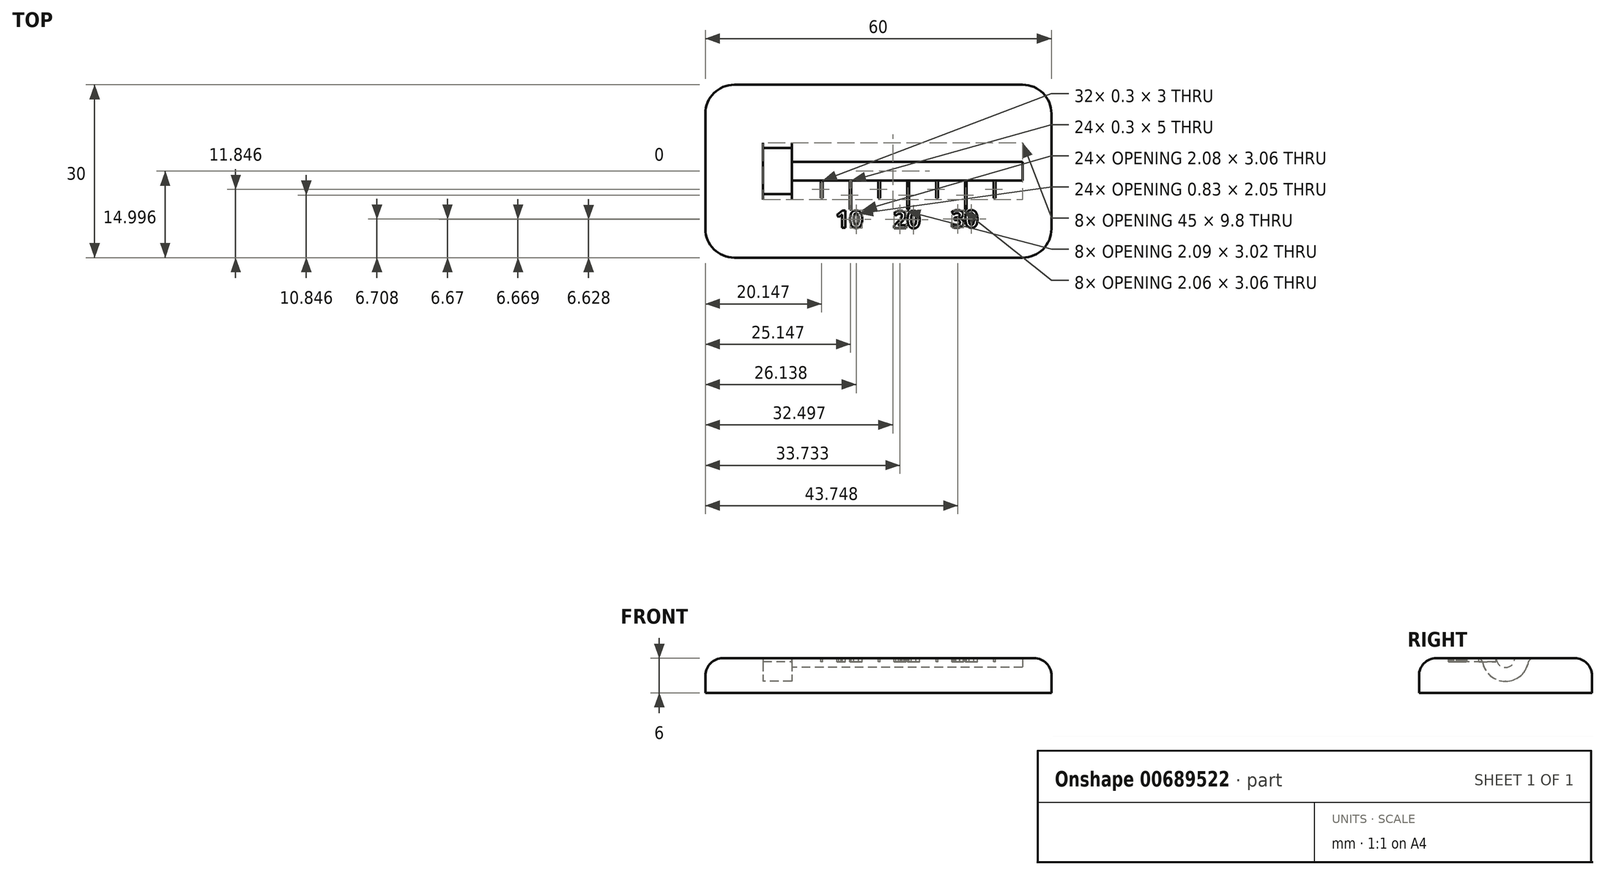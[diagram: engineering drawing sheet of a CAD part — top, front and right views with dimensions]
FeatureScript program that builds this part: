
annotation { "Feature Type Name" : "Feature", "Feature Type Description" : "" }
export const myFeature = defineFeature(function(context is Context, id is Id, definition is map)
    precondition{}
    {
        {
            var Q0;
            Q0=qCreatedBy(makeId("Top.planeOp"),FACE);
            var sketch = newSketch(context, id + "F0", { "sketchPlane" : qUnion([Q0])});
            skLineSegment(sketch, "E0.bottom", {"start": v(-3.5, 3.1) * mm, "end": v(56.5, 3.1) * mm});
            skLineSegment(sketch, "E0.top", {"start": v(-3.5, -26.9) * mm, "end": v(56.5, -26.9) * mm});
            skLineSegment(sketch, "E0.left", {"start": v(-3.5, 3.1) * mm, "end": v(-3.5, -26.9) * mm});
            skLineSegment(sketch, "E0.right", {"start": v(56.5, 3.1) * mm, "end": v(56.5, -26.9) * mm});
            skSolve(sketch);
        }
        {
            var Q0;
            Q0=makeQuery(id+"F0.imprint","IMPRINT",FACE,{"disambiguationData":[TD([[makeQuery(id+"F0.imprint","IMPRINT",EDGE,{"derivedFrom":sQuery(id+"F0.wireOp",EDGE,"E0.bottom")}),-1.0]])]});
            extrude(context, id + "F1", {"entities" : qUnion([Q0]), "depth" : 6 * mm, "offsetDistance" : 25 * mm});
        }
        {
            var Q0;
            Q0=makeQuery(id+"F1.opExtrude","CAP_FACE",FACE,{"disambiguationData":[OSD([sQuery(id+"F0.wireOp",EDGE,"E0.bottom"),sQuery(id+"F0.wireOp",EDGE,"E0.top"),sQuery(id+"F0.wireOp",EDGE,"E0.left"),sQuery(id+"F0.wireOp",EDGE,"E0.right")])],"isStart":false});
            var sketch = newSketch(context, id + "F2", { "sketchPlane" : qUnion([Q0])});
            skLineSegment(sketch, "E1.bottom", {"start": v(51.5, -10.24) * mm, "end": v(11.5, -10.24) * mm});
            skLineSegment(sketch, "E1.top", {"start": v(51.5, -13.54) * mm, "end": v(11.5, -13.54) * mm});
            skLineSegment(sketch, "E1.left", {"start": v(51.5, -10.24) * mm, "end": v(51.5, -13.54) * mm});
            skLineSegment(sketch, "E1.right", {"start": v(11.5, -10.24) * mm, "end": v(11.5, -13.54) * mm});
            skLineSegment(sketch, "E2", {"start": v(31.5, -10.24) * mm, "end": v(31.5, 3.1) * mm, "construction": true});
            skLineSegment(sketch, "E3", {"start": v(31.5, -13.54) * mm, "end": v(31.5, -26.9) * mm, "construction": true});
            skSolve(sketch);
        }
        {
            var Q0;
            Q0=makeQuery(id+"F2.imprint","IMPRINT",FACE,{"disambiguationData":[TD([[makeQuery(id+"F2.imprint","IMPRINT",EDGE,{"derivedFrom":sQuery(id+"F2.wireOp",EDGE,"E1.bottom")}),-1.0]])]});
            var sketch = newSketch(context, id + "F3", { "sketchPlane" : qUnion([Q0])});
            skLineSegment(sketch, "E4.bottom", {"start": v(11.5, -7.9) * mm, "end": v(6.5, -7.9) * mm});
            skLineSegment(sketch, "E4.top", {"start": v(11.5, -15.9) * mm, "end": v(6.5, -15.9) * mm});
            skLineSegment(sketch, "E4.left", {"start": v(11.5, -7.9) * mm, "end": v(11.5, -15.9) * mm});
            skLineSegment(sketch, "E4.right", {"start": v(6.5, -7.9) * mm, "end": v(6.5, -15.9) * mm});
            skLineSegment(sketch, "E5", {"start": v(9, -7.9) * mm, "end": v(9, 3.1) * mm, "construction": true});
            skLineSegment(sketch, "E6", {"start": v(9, -15.9) * mm, "end": v(9, -26.9) * mm, "construction": true});
            skSolve(sketch);
        }
        {
            var Q0;
            {var subQ3=sQuery(id+"F3.wireOp",EDGE,"E4.bottom");Q0=makeQuery(id+"F3.imprint","IMPRINT",FACE,{"disambiguationData":[TD([[makeQuery(id+"F3.imprint","IMPRINT",EDGE,{"derivedFrom":subQ3}),1.0]])]});}
            extrude(context, id + "F4", {"entities" : qUnion([Q0]), "operationType" : NewBodyOperationType.REMOVE, "oppositeDirection" : true, "depth" : 4 * mm, "offsetDistance" : 25 * mm});
        }
        {
            var Q0;
            Q0=makeQuery(id+"F4.boolean.opBoolean","COPY",FACE,{"derivedFrom":makeQuery(id+"F4.opExtrude","SWEPT_FACE",FACE,{"disambiguationData":[OSD([sQuery(id+"F3.wireOp",EDGE,"E4.left")])]})});
            var sketch = newSketch(context, id + "F5", { "sketchPlane" : qUnion([Q0])});
            skArc(sketch, "E7", {"start": v(10.3, 6) * mm, "mid": v(11.9, 4.4) * mm, "end": v(13.5, 6) * mm});
            skLineSegment(sketch, "E8", {"start": v(11.9, 6) * mm, "end": v(7.9, 6) * mm, "construction": true});
            skLineSegment(sketch, "E9", {"start": v(11.9, 6) * mm, "end": v(15.9, 6) * mm, "construction": true});
            skSolve(sketch);
        }
        {
            var Q0;
            {var subQ0=sQuery(id+"F5.wireOp",EDGE,"E7");Q0=makeQuery(id+"F5.imprint","IMPRINT",FACE,{"disambiguationData":[TD([[makeQuery(id+"F5.imprint","IMPRINT",EDGE,{"derivedFrom":subQ0}),1.0]])]});}
            extrude(context, id + "F6", {"entities" : qUnion([Q0]), "operationType" : NewBodyOperationType.REMOVE, "oppositeDirection" : true, "depth" : 40 * mm, "offsetDistance" : 25 * mm});
        }
        {
            var Q0;
            Q0=makeQuery(id+"F4.boolean.opBoolean","COPY",EDGE,{"derivedFrom":makeQuery(id+"F4.opExtrude","CAP_EDGE",EDGE,{"disambiguationData":[OSD([sQuery(id+"F3.wireOp",EDGE,"E4.top")])],"isStart":false})});
            var Q1;
            Q1=makeQuery(id+"F4.boolean.opBoolean","COPY",EDGE,{"derivedFrom":makeQuery(id+"F4.opExtrude","CAP_EDGE",EDGE,{"disambiguationData":[OSD([sQuery(id+"F3.wireOp",EDGE,"E4.bottom")])],"isStart":false})});
            fillet(context, id + "F7", {"entities" : qUnion([Q0, Q1]), "radius" : 4 * mm, "tangentPropagation" : true, "allowEdgeOverflow" : false});
        }
        {
            var Q0;
            Q0=makeQuery(id+"F7.opFillet","BLEND_EDGE",EDGE,{"blendedFrom":[makeQuery(id+"F4.boolean.opBoolean","COPY",EDGE,{"derivedFrom":makeQuery(id+"F4.opExtrude","CAP_EDGE",EDGE,{"disambiguationData":[OSD([sQuery(id+"F3.wireOp",EDGE,"E4.bottom")])],"isStart":false})}),makeQuery(id+"F1.opExtrude","CAP_FACE",FACE,{"disambiguationData":[OSD([sQuery(id+"F0.wireOp",EDGE,"E0.bottom"),sQuery(id+"F0.wireOp",EDGE,"E0.top"),sQuery(id+"F0.wireOp",EDGE,"E0.left"),sQuery(id+"F0.wireOp",EDGE,"E0.right")])],"isStart":false})],"blendedInto":[makeQuery(id+"F1.opExtrude","CAP_FACE",FACE,{"disambiguationData":[OSD([sQuery(id+"F0.wireOp",EDGE,"E0.bottom"),sQuery(id+"F0.wireOp",EDGE,"E0.top"),sQuery(id+"F0.wireOp",EDGE,"E0.left"),sQuery(id+"F0.wireOp",EDGE,"E0.right")])],"isStart":false})]});
            var Q1;
            Q1=makeQuery(id+"F7.opFillet","BLEND_EDGE",EDGE,{"blendedFrom":[makeQuery(id+"F4.boolean.opBoolean","COPY",EDGE,{"derivedFrom":makeQuery(id+"F4.opExtrude","CAP_EDGE",EDGE,{"disambiguationData":[OSD([sQuery(id+"F3.wireOp",EDGE,"E4.top")])],"isStart":false})}),makeQuery(id+"F1.opExtrude","CAP_FACE",FACE,{"disambiguationData":[OSD([sQuery(id+"F0.wireOp",EDGE,"E0.bottom"),sQuery(id+"F0.wireOp",EDGE,"E0.top"),sQuery(id+"F0.wireOp",EDGE,"E0.left"),sQuery(id+"F0.wireOp",EDGE,"E0.right")])],"isStart":false})],"blendedInto":[makeQuery(id+"F1.opExtrude","CAP_FACE",FACE,{"disambiguationData":[OSD([sQuery(id+"F0.wireOp",EDGE,"E0.bottom"),sQuery(id+"F0.wireOp",EDGE,"E0.top"),sQuery(id+"F0.wireOp",EDGE,"E0.left"),sQuery(id+"F0.wireOp",EDGE,"E0.right")])],"isStart":false})]});
            var Q2;
            Q2=makeQuery(id+"F4.boolean.opBoolean","COPY",EDGE,{"derivedFrom":makeQuery(id+"F4.opExtrude","CAP_EDGE",EDGE,{"disambiguationData":[OSD([sQuery(id+"F3.wireOp",EDGE,"E4.right")])],"isStart":true})});
            fillet(context, id + "F8", {"entities" : qUnion([Q0, Q1, Q2]), "radius" : 1 * mm, "tangentPropagation" : true, "allowEdgeOverflow" : false});
        }
        {
            var Q0;
            Q0=makeQuery(id+"F2.imprint","IMPRINT",FACE,{"disambiguationData":[TD([[makeQuery(id+"F2.imprint","IMPRINT",EDGE,{"derivedFrom":sQuery(id+"F2.wireOp",EDGE,"E1.bottom")}),-1.0]])]});
            var sketch = newSketch(context, id + "F9", { "sketchPlane" : qUnion([Q0])});
            skLineSegment(sketch, "E10.bottom", {"start": v(21.5, -13.54) * mm, "end": v(21.8, -13.54) * mm});
            skLineSegment(sketch, "E10.top", {"start": v(21.5, -18.54) * mm, "end": v(21.8, -18.54) * mm});
            skLineSegment(sketch, "E10.left", {"start": v(21.5, -13.54) * mm, "end": v(21.5, -18.54) * mm});
            skLineSegment(sketch, "E10.right", {"start": v(21.8, -13.54) * mm, "end": v(21.8, -18.54) * mm});
            skLineSegment(sketch, "E11.bottom", {"start": v(31.5, -13.54) * mm, "end": v(31.8, -13.54) * mm});
            skLineSegment(sketch, "E11.top", {"start": v(31.5, -18.54) * mm, "end": v(31.8, -18.54) * mm});
            skLineSegment(sketch, "E11.left", {"start": v(31.5, -13.54) * mm, "end": v(31.5, -18.54) * mm});
            skLineSegment(sketch, "E11.right", {"start": v(31.8, -13.54) * mm, "end": v(31.8, -18.54) * mm});
            skLineSegment(sketch, "E12.bottom", {"start": v(41.8, -18.54) * mm, "end": v(41.5, -18.54) * mm});
            skLineSegment(sketch, "E12.top", {"start": v(41.8, -13.54) * mm, "end": v(41.5, -13.54) * mm});
            skLineSegment(sketch, "E12.left", {"start": v(41.8, -18.54) * mm, "end": v(41.8, -13.54) * mm});
            skLineSegment(sketch, "E12.right", {"start": v(41.5, -18.54) * mm, "end": v(41.5, -13.54) * mm});
            skLineSegment(sketch, "E13.bottom", {"start": v(16.5, -13.54) * mm, "end": v(16.8, -13.54) * mm});
            skLineSegment(sketch, "E13.top", {"start": v(16.5, -16.54) * mm, "end": v(16.8, -16.54) * mm});
            skLineSegment(sketch, "E13.left", {"start": v(16.5, -13.54) * mm, "end": v(16.5, -16.54) * mm});
            skLineSegment(sketch, "E13.right", {"start": v(16.8, -13.54) * mm, "end": v(16.8, -16.54) * mm});
            skLineSegment(sketch, "E14.bottom", {"start": v(26.8, -16.54) * mm, "end": v(26.5, -16.54) * mm});
            skLineSegment(sketch, "E14.top", {"start": v(26.8, -13.54) * mm, "end": v(26.5, -13.54) * mm});
            skLineSegment(sketch, "E14.left", {"start": v(26.8, -16.54) * mm, "end": v(26.8, -13.54) * mm});
            skLineSegment(sketch, "E14.right", {"start": v(26.5, -16.54) * mm, "end": v(26.5, -13.54) * mm});
            skLineSegment(sketch, "E15.bottom", {"start": v(36.8, -16.54) * mm, "end": v(36.5, -16.54) * mm});
            skLineSegment(sketch, "E15.top", {"start": v(36.8, -13.54) * mm, "end": v(36.5, -13.54) * mm});
            skLineSegment(sketch, "E15.left", {"start": v(36.8, -16.54) * mm, "end": v(36.8, -13.54) * mm});
            skLineSegment(sketch, "E15.right", {"start": v(36.5, -16.54) * mm, "end": v(36.5, -13.54) * mm});
            skLineSegment(sketch, "E16.bottom", {"start": v(46.8, -16.54) * mm, "end": v(46.5, -16.54) * mm});
            skLineSegment(sketch, "E16.top", {"start": v(46.8, -13.54) * mm, "end": v(46.5, -13.54) * mm});
            skLineSegment(sketch, "E16.left", {"start": v(46.8, -16.54) * mm, "end": v(46.8, -13.54) * mm});
            skLineSegment(sketch, "E16.right", {"start": v(46.5, -16.54) * mm, "end": v(46.5, -13.54) * mm});
            skText(sketch, "E17", { "text": "10", "fontName": "OpenSans-Bold.ttf"});
            skText(sketch, "E18", { "text": "20", "fontName": "OpenSans-Bold.ttf"});
            skText(sketch, "E19", { "text": "30", "fontName": "OpenSans-Bold.ttf"});
            const initialGuessF9  = {"E17": [0.01907, -0.02171, 1, 0, 0.003], "E18": [0.02903, -0.02177, 1, 0, 0.003], "E19": [0.03906, -0.02167, 1, 0, 0.003]};
            skSetInitialGuess(sketch, initialGuessF9);
            skSolve(sketch);
        }
        {
            var Q0;
            Q0 = qSketchRegion(id + "F9", true);
            extrude(context, id + "F10", {"entities" : qUnion([Q0]), "operationType" : NewBodyOperationType.REMOVE, "oppositeDirection" : true, "depth" : 0.6 * mm, "offsetDistance" : 25 * mm});
        }
        {
            var Q0;
            Q0=makeQuery(id+"F1.opExtrude","CAP_EDGE",EDGE,{"disambiguationData":[OSD([sQuery(id+"F0.wireOp",EDGE,"E0.bottom")])],"isStart":false});
            var Q1;
            Q1=makeQuery(id+"F1.opExtrude","CAP_EDGE",EDGE,{"disambiguationData":[OSD([sQuery(id+"F0.wireOp",EDGE,"E0.left")])],"isStart":false});
            var Q2;
            Q2=makeQuery(id+"F1.opExtrude","CAP_EDGE",EDGE,{"disambiguationData":[OSD([sQuery(id+"F0.wireOp",EDGE,"E0.top")])],"isStart":false});
            var Q3;
            Q3=makeQuery(id+"F1.opExtrude","CAP_EDGE",EDGE,{"disambiguationData":[OSD([sQuery(id+"F0.wireOp",EDGE,"E0.right")])],"isStart":false});
            fillet(context, id + "F11", {"entities" : qUnion([Q0, Q1, Q2, Q3]), "radius" : 3 * mm, "tangentPropagation" : true, "allowEdgeOverflow" : false});
        }
        {
            var Q0;
            Q0=makeQuery(id+"F1.opExtrude","SWEPT_EDGE",EDGE,{"disambiguationData":[OSD([sQuery(id+"F0.wireOp",EDGE,"E0.top"),sQuery(id+"F0.wireOp",EDGE,"E0.left")])]});
            var Q1;
            Q1=makeQuery(id+"F1.opExtrude","SWEPT_EDGE",EDGE,{"disambiguationData":[OSD([sQuery(id+"F0.wireOp",EDGE,"E0.top"),sQuery(id+"F0.wireOp",EDGE,"E0.right")])]});
            var Q2;
            Q2=makeQuery(id+"F1.opExtrude","SWEPT_EDGE",EDGE,{"disambiguationData":[OSD([sQuery(id+"F0.wireOp",EDGE,"E0.bottom"),sQuery(id+"F0.wireOp",EDGE,"E0.left")])]});
            var Q3;
            Q3=makeQuery(id+"F1.opExtrude","SWEPT_EDGE",EDGE,{"disambiguationData":[OSD([sQuery(id+"F0.wireOp",EDGE,"E0.bottom"),sQuery(id+"F0.wireOp",EDGE,"E0.right")])]});
            fillet(context, id + "F12", {"entities" : qUnion([Q0, Q1, Q2, Q3]), "radius" : 5 * mm, "tangentPropagation" : true, "allowEdgeOverflow" : false});
        }
    });
